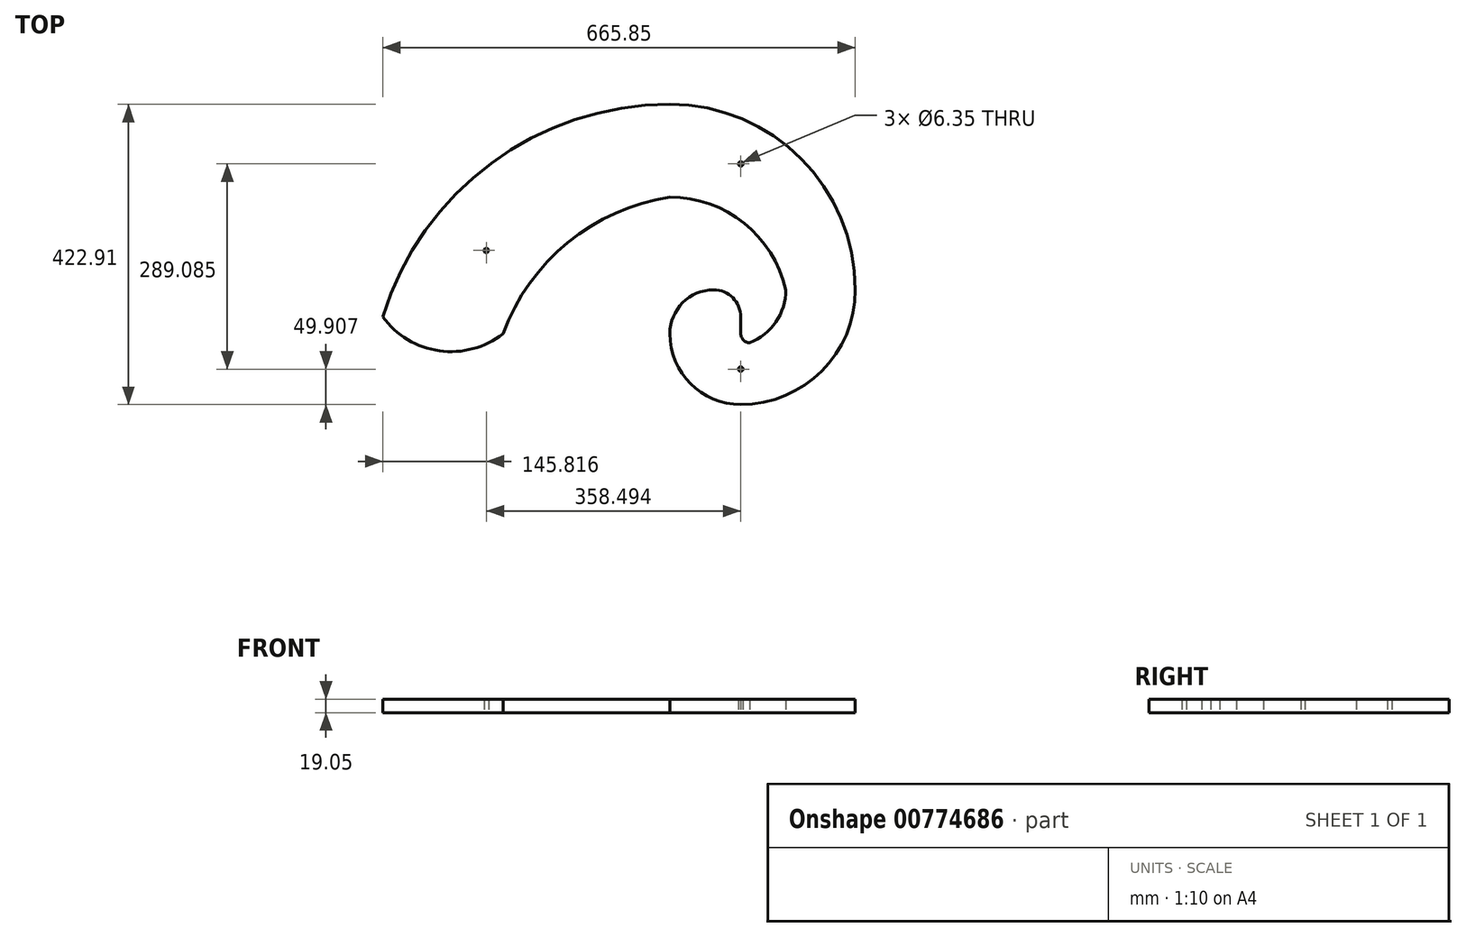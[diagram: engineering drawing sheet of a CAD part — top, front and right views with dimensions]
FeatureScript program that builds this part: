
annotation { "Feature Type Name" : "Feature", "Feature Type Description" : "" }
export const myFeature = defineFeature(function(context is Context, id is Id, definition is map)
    precondition{}
    {
        {
            var Q0;
            Q0=qCreatedBy(makeId("Top.planeOp"),FACE);
            var sketch = newSketch(context, id + "F0", { "sketchPlane" : qUnion([Q0])});
            skLineSegment(sketch, "E0.bottom", {"start": v(0, 0) * mm, "end": v(38.1, 0) * mm, "construction": true});
            skLineSegment(sketch, "E0.top", {"start": v(0, 38.1) * mm, "end": v(38.1, 38.1) * mm, "construction": true});
            skLineSegment(sketch, "E0.left", {"start": v(0, 0) * mm, "end": v(0, 38.1) * mm, "construction": true});
            skLineSegment(sketch, "E0.right", {"start": v(38.1, 0) * mm, "end": v(38.1, 38.1) * mm, "construction": true});
            skLineSegment(sketch, "E1.bottom", {"start": v(0, 38.1) * mm, "end": v(-61.72, 38.1) * mm, "construction": true});
            skLineSegment(sketch, "E1.top", {"start": v(0, -23.62) * mm, "end": v(-61.72, -23.62) * mm, "construction": true});
            skLineSegment(sketch, "E1.left", {"start": v(0, 38.1) * mm, "end": v(0, -23.62) * mm, "construction": true});
            skLineSegment(sketch, "E1.right", {"start": v(-61.72, 38.1) * mm, "end": v(-61.72, -23.62) * mm, "construction": true});
            skLineSegment(sketch, "E2.bottom", {"start": v(-61.72, -23.62) * mm, "end": v(38.1, -23.62) * mm, "construction": true});
            skLineSegment(sketch, "E2.top", {"start": v(-61.72, -123.44) * mm, "end": v(38.1, -123.44) * mm, "construction": true});
            skLineSegment(sketch, "E2.left", {"start": v(-61.72, -23.62) * mm, "end": v(-61.72, -123.44) * mm, "construction": true});
            skLineSegment(sketch, "E2.right", {"start": v(38.1, -23.62) * mm, "end": v(38.1, -123.44) * mm, "construction": true});
            skLineSegment(sketch, "E3.bottom", {"start": v(38.1, -123.44) * mm, "end": v(199.64, -123.44) * mm, "construction": true});
            skLineSegment(sketch, "E3.top", {"start": v(38.1, 38.1) * mm, "end": v(199.64, 38.1) * mm, "construction": true});
            skLineSegment(sketch, "E3.left", {"start": v(38.1, -123.44) * mm, "end": v(38.1, 38.1) * mm, "construction": true});
            skLineSegment(sketch, "E3.right", {"start": v(199.64, -123.44) * mm, "end": v(199.64, 38.1) * mm, "construction": true});
            skLineSegment(sketch, "E4.bottom", {"start": v(199.64, 38.1) * mm, "end": v(-61.72, 38.1) * mm, "construction": true});
            skLineSegment(sketch, "E4.top", {"start": v(199.64, 299.47) * mm, "end": v(-61.72, 299.47) * mm, "construction": true});
            skLineSegment(sketch, "E4.left", {"start": v(199.64, 38.1) * mm, "end": v(199.64, 299.47) * mm, "construction": true});
            skLineSegment(sketch, "E4.right", {"start": v(-61.72, 38.1) * mm, "end": v(-61.72, 299.47) * mm, "construction": true});
            skLineSegment(sketch, "E5.bottom", {"start": v(-61.72, -123.44) * mm, "end": v(-484.63, -123.44) * mm, "construction": true});
            skLineSegment(sketch, "E5.top", {"start": v(-61.72, 299.13) * mm, "end": v(-484.63, 299.13) * mm, "construction": true});
            skLineSegment(sketch, "E5.left", {"start": v(-61.72, -123.44) * mm, "end": v(-61.72, 299.13) * mm, "construction": true});
            skLineSegment(sketch, "E5.right", {"start": v(-484.63, -123.44) * mm, "end": v(-484.63, 299.13) * mm, "construction": true});
            skArc(sketch, "E6", {"start": v(38.1, 0) * mm, "mid": v(26.94, 26.94) * mm, "end": v(0, 38.1) * mm});
            skArc(sketch, "E7", {"start": v(0, 38.1) * mm, "mid": v(-43.64, 20.02) * mm, "end": v(-61.72, -23.62) * mm});
            skArc(sketch, "E8", {"start": v(-61.72, -23.62) * mm, "mid": v(-32.48, -94.2) * mm, "end": v(38.1, -123.44) * mm});
            skArc(sketch, "E9", {"start": v(38.1, -123.44) * mm, "mid": v(152.33, -76.13) * mm, "end": v(199.64, 38.1) * mm});
            skArc(sketch, "E10", {"start": v(199.64, 38.1) * mm, "mid": v(123.1, 222.91) * mm, "end": v(-61.72, 299.47) * mm});
            skArc(sketch, "E11", {"start": v(-61.72, 299.47) * mm, "mid": v(-360.76, 175.6) * mm, "end": v(-484.63, -123.44) * mm});
            skLineSegment(sketch, "E12", {"start": v(38.1, 0) * mm, "end": v(38.1, -23.62) * mm});
            skLineSegment(sketch, "E13.bottom", {"start": v(38.1, -23.62) * mm, "end": v(50.8, -23.62) * mm, "construction": true});
            skLineSegment(sketch, "E13.top", {"start": v(38.1, -36.32) * mm, "end": v(50.8, -36.32) * mm, "construction": true});
            skLineSegment(sketch, "E13.left", {"start": v(38.1, -23.62) * mm, "end": v(38.1, -36.32) * mm, "construction": true});
            skLineSegment(sketch, "E13.right", {"start": v(50.8, -23.62) * mm, "end": v(50.8, -36.32) * mm, "construction": true});
            skArc(sketch, "E14", {"start": v(38.1, -23.62) * mm, "mid": v(41.82, -32.6) * mm, "end": v(50.8, -36.32) * mm});
            skLineSegment(sketch, "E15.bottom", {"start": v(50.8, -36.32) * mm, "end": v(101.66, -36.32) * mm, "construction": true});
            skLineSegment(sketch, "E15.top", {"start": v(50.8, 38.1) * mm, "end": v(101.66, 38.1) * mm, "construction": true});
            skLineSegment(sketch, "E15.left", {"start": v(50.8, -36.32) * mm, "end": v(50.8, 38.1) * mm, "construction": true});
            skLineSegment(sketch, "E15.right", {"start": v(101.66, -36.32) * mm, "end": v(101.66, 38.1) * mm, "construction": true});
            skArc(sketch, "E16", {"start": v(50.8, -36.32) * mm, "mid": v(87.73, -6.97) * mm, "end": v(101.66, 38.1) * mm});
            skLineSegment(sketch, "E17.bottom", {"start": v(101.66, 38.1) * mm, "end": v(-61.72, 38.1) * mm, "construction": true});
            skLineSegment(sketch, "E17.top", {"start": v(101.66, 168.78) * mm, "end": v(-61.72, 168.78) * mm, "construction": true});
            skLineSegment(sketch, "E17.left", {"start": v(101.66, 38.1) * mm, "end": v(101.66, 168.78) * mm, "construction": true});
            skLineSegment(sketch, "E17.right", {"start": v(-61.72, 38.1) * mm, "end": v(-61.72, 168.78) * mm, "construction": true});
            skArc(sketch, "E18", {"start": v(101.66, 38.1) * mm, "mid": v(42.89, 132.1) * mm, "end": v(-61.72, 168.78) * mm});
            skLineSegment(sketch, "E19.bottom", {"start": v(-61.72, -23.62) * mm, "end": v(-296.68, -23.62) * mm, "construction": true});
            skLineSegment(sketch, "E19.top", {"start": v(-61.72, 168.78) * mm, "end": v(-296.68, 168.78) * mm, "construction": true});
            skLineSegment(sketch, "E19.left", {"start": v(-61.72, -23.62) * mm, "end": v(-61.72, 168.78) * mm, "construction": true});
            skLineSegment(sketch, "E19.right", {"start": v(-296.68, -23.62) * mm, "end": v(-296.68, 168.78) * mm, "construction": true});
            skArc(sketch, "E20", {"start": v(-61.72, 168.78) * mm, "mid": v(-205.52, 104.72) * mm, "end": v(-296.68, -23.62) * mm});
            skArc(sketch, "E21", {"start": v(-466.21, 0) * mm, "mid": v(-386.46, -47.76) * mm, "end": v(-296.68, -23.62) * mm});
            skLineSegment(sketch, "E22", {"start": v(38.1, -73.53) * mm, "end": v(199.64, -73.53) * mm, "construction": true});
            skLineSegment(sketch, "E23", {"start": v(38.1, 38.1) * mm, "end": v(38.1, 299.47) * mm, "construction": true});
            skCircle(sketch, "E24", {"center": v(38.1, 215.55) * mm, "radius": 3.17 * mm});
            skCircle(sketch, "E25", {"center": v(-320.4, 93.51) * mm, "radius": 3.18 * mm});
            skCircle(sketch, "E26", {"center": v(38.1, -73.53) * mm, "radius": 3.18 * mm});
            skSolve(sketch);
        }
        {
            var Q0;
            Q0=makeQuery(id+"F0.imprint","IMPRINT",FACE,{"disambiguationData":[TD([[makeQuery(id+"F0.imprint","IMPRINT",EDGE,{"derivedFrom":sQuery(id+"F0.wireOp",EDGE,"E6")}),1.0]])]});
            extrude(context, id + "F1", {"entities" : qUnion([Q0]), "depth" : 19.05 * mm, "offsetDistance" : 25.4 * mm});
        }
    });
